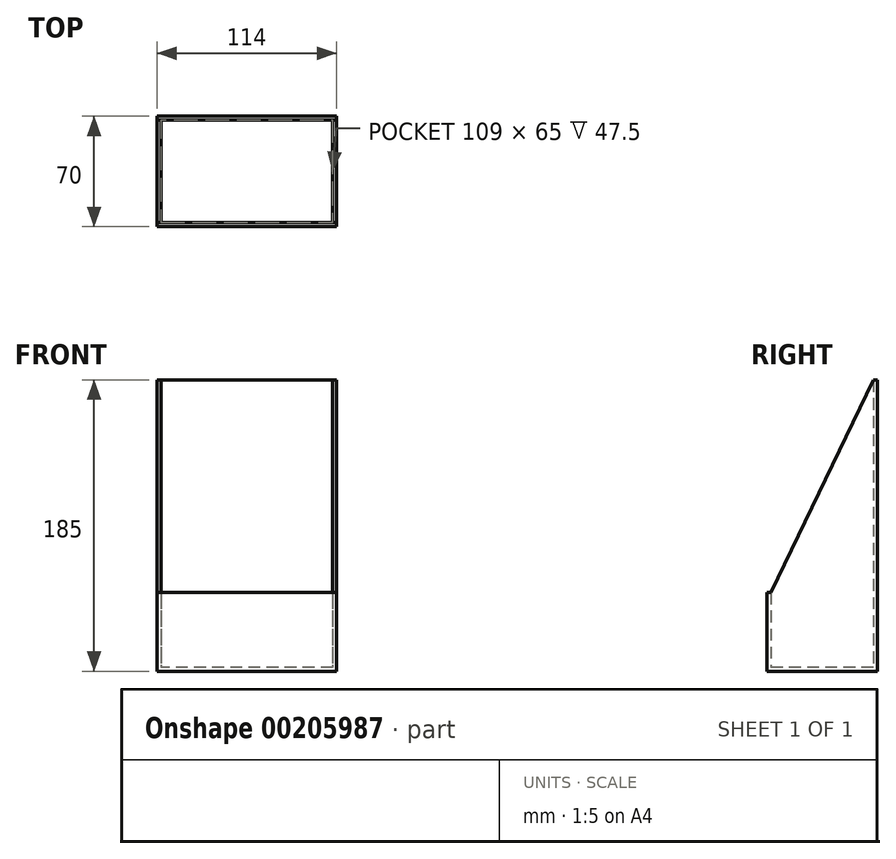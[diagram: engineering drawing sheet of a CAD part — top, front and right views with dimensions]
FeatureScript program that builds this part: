
annotation { "Feature Type Name" : "Feature", "Feature Type Description" : "" }
export const myFeature = defineFeature(function(context is Context, id is Id, definition is map)
    precondition{}
    {
        {
            var Q0;
            Q0=qCreatedBy(makeId("Top.planeOp"),FACE);
            var sketch = newSketch(context, id + "F0", { "sketchPlane" : qUnion([Q0])});
            skLineSegment(sketch, "E0.bottom", {"start": v(0, 0) * mm, "end": v(-114, 0) * mm});
            skLineSegment(sketch, "E0.top", {"start": v(0, -70) * mm, "end": v(-114, -70) * mm});
            skLineSegment(sketch, "E0.left", {"start": v(0, 0) * mm, "end": v(0, -70) * mm});
            skLineSegment(sketch, "E0.right", {"start": v(-114, 0) * mm, "end": v(-114, -70) * mm});
            skSolve(sketch);
        }
        {
            var Q0;
            Q0 = qSketchRegion(id + "F0", true);
            extrude(context, id + "F1", {"entities" : qUnion([Q0]), "depth" : 185 * mm});
        }
        {
            var Q0;
            Q0=qCreatedBy(makeId("Top.planeOp"),FACE);
            cPlane(context, id + "F2", {"entities" : qUnion([Q0]), "cplaneType" : CPlaneType.OFFSET, "offset" : 2.5 * mm, "width" : 150 * mm, "height" : 150 * mm});
        }
        {
            var Q0;
            Q0=qCreatedBy(id+"F2.planeOp",FACE);
            var sketch = newSketch(context, id + "F3", { "sketchPlane" : qUnion([Q0])});
            skLineSegment(sketch, "E1.0", {"start": v(0, -70) * mm, "end": v(-114, -70) * mm, "construction": true});
            skLineSegment(sketch, "E1.1", {"start": v(-114, 0) * mm, "end": v(-114, -70) * mm, "construction": true});
            skLineSegment(sketch, "E1.2", {"start": v(0, 0) * mm, "end": v(-114, 0) * mm, "construction": true});
            skLineSegment(sketch, "E1.3", {"start": v(0, 0) * mm, "end": v(0, -70) * mm, "construction": true});
            skLineSegment(sketch, "E2.0", {"start": v(-2.5, -2.5) * mm, "end": v(-111.5, -2.5) * mm});
            skLineSegment(sketch, "E2.1", {"start": v(-2.5, -2.5) * mm, "end": v(-2.5, -67.5) * mm});
            skLineSegment(sketch, "E2.2", {"start": v(-2.5, -67.5) * mm, "end": v(-111.5, -67.5) * mm});
            skLineSegment(sketch, "E2.3", {"start": v(-111.5, -2.5) * mm, "end": v(-111.5, -67.5) * mm});
            skSolve(sketch);
        }
        {
            var Q0;
            Q0=qCreatedBy(makeId("Right.planeOp"),FACE);
            var sketch = newSketch(context, id + "F4", { "sketchPlane" : qUnion([Q0])});
            skLineSegment(sketch, "E3.0", {"start": v(0, 0) * mm, "end": v(-70, 0) * mm, "construction": true});
            skLineSegment(sketch, "E4.0", {"start": v(0, 50) * mm, "end": v(-70, 50) * mm, "construction": true});
            skLineSegment(sketch, "E5.0", {"start": v(0, 185) * mm, "end": v(-70, 185) * mm, "construction": true});
            skLineSegment(sketch, "E6", {"start": v(-70, 50) * mm, "end": v(-67.5, 50) * mm});
            skLineSegment(sketch, "E7", {"start": v(-67.5, 50) * mm, "end": v(-2.5, 185) * mm});
            skLineSegment(sketch, "E8", {"start": v(-2.5, 185) * mm, "end": v(0, 185) * mm});
            skLineSegment(sketch, "E9", {"start": v(-2.5, 185) * mm, "end": v(-70, 185) * mm});
            skLineSegment(sketch, "E10", {"start": v(-70, 50) * mm, "end": v(-70, 185) * mm});
            skLineSegment(sketch, "E11", {"start": v(-70, 185) * mm, "end": v(-2.5, 185) * mm});
            skSolve(sketch);
        }
        {
            var Q0;
            Q0 = qSketchRegion(id + "F4", true);
            var Q1;
            Q1=makeQuery(id+"F1.opExtrude","SWEPT_FACE",FACE,{"disambiguationData":[OSD([sQuery(id+"F0.wireOp",EDGE,"E0.right")])]});
            extrude(context, id + "F5", {"entities" : qUnion([Q0]), "operationType" : NewBodyOperationType.REMOVE, "endBound" : BoundingType.UP_TO_SURFACE, "oppositeDirection" : true, "endBoundEntityFace" : qUnion([Q1]), "depth" : 25 * mm});
        }
        {
            var Q0;
            Q0 = qSketchRegion(id + "F3", true);
            extrude(context, id + "F6", {"entities" : qUnion([Q0]), "operationType" : NewBodyOperationType.REMOVE, "endBound" : BoundingType.THROUGH_ALL, "depth" : 25 * mm});
        }
    });
